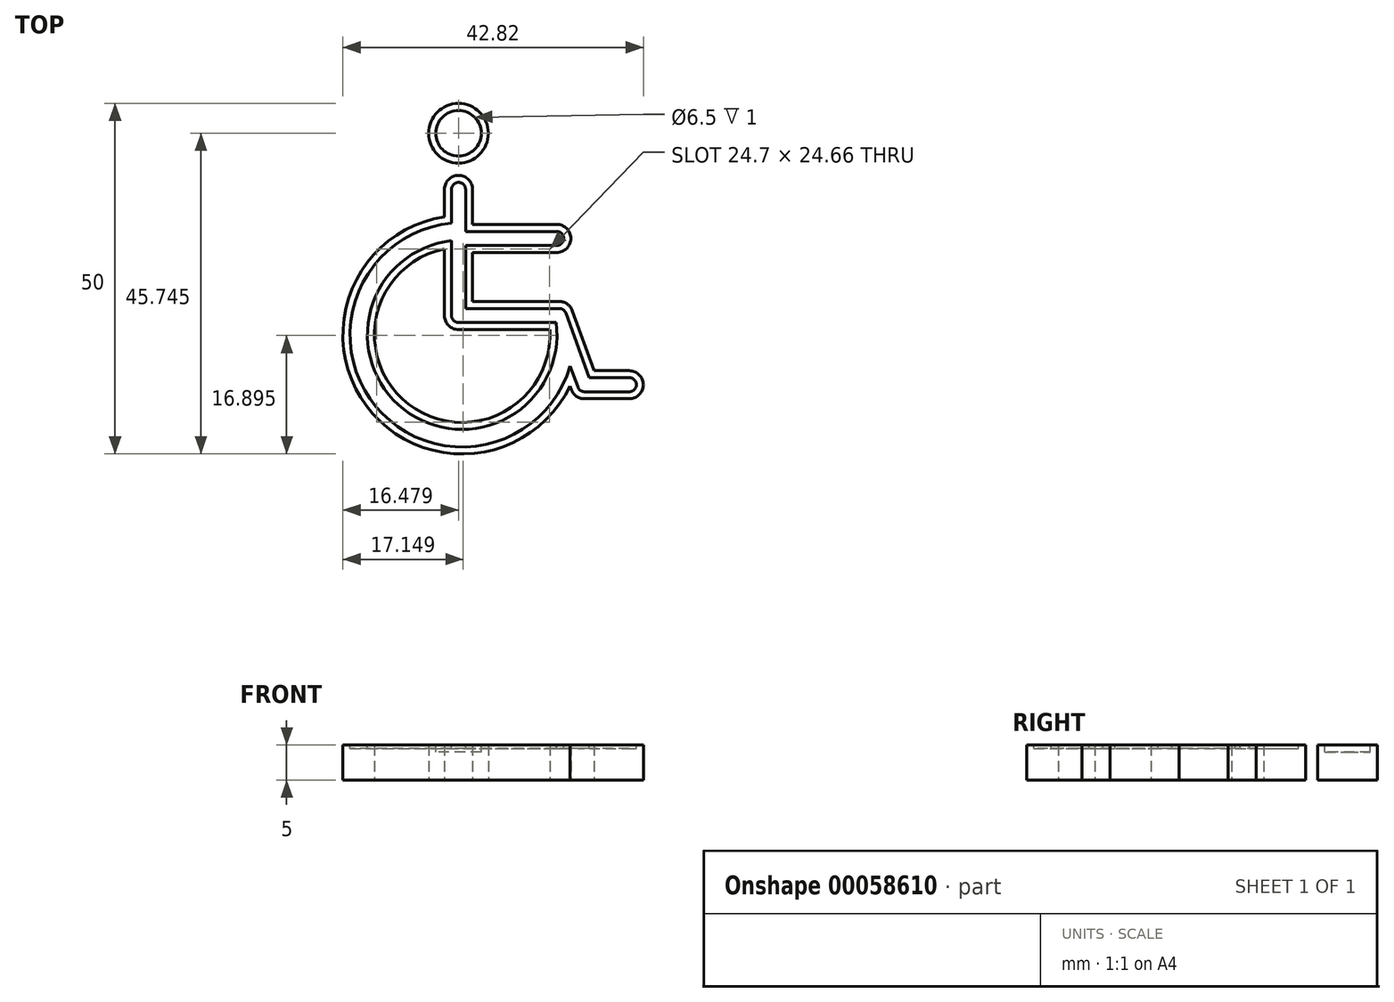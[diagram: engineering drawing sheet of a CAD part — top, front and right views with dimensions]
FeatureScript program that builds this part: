
annotation { "Feature Type Name" : "Feature", "Feature Type Description" : "" }
export const myFeature = defineFeature(function(context is Context, id is Id, definition is map)
    precondition{}
    {
        {
            var Q0;
            Q0=qCreatedBy(makeId("Top.planeOp"),FACE);
            var sketch = newSketch(context, id + "F0", { "sketchPlane" : qUnion([Q0])});
            skLineSegment(sketch, "E0", {"start": v(22.08, 21.62) * mm, "end": v(35.83, 21.62) * mm});
            skLineSegment(sketch, "E1", {"start": v(39.42, 11.75) * mm, "end": v(35.83, 21.62) * mm});
            skLineSegment(sketch, "E2", {"start": v(39.42, 11.75) * mm, "end": v(46.42, 11.75) * mm});
            skLineSegment(sketch, "E3", {"start": v(46.42, 11.75) * mm, "end": v(46.42, 7.75) * mm});
            skLineSegment(sketch, "E4", {"start": v(46.42, 7.75) * mm, "end": v(36.62, 7.75) * mm});
            skLineSegment(sketch, "E5", {"start": v(36.62, 7.75) * mm, "end": v(35.96, 9.57) * mm});
            skLineSegment(sketch, "E6", {"start": v(22.08, 21.62) * mm, "end": v(22.08, 28.62) * mm});
            skLineSegment(sketch, "E7", {"start": v(22.08, 28.62) * mm, "end": v(36.08, 28.62) * mm});
            skLineSegment(sketch, "E8", {"start": v(36.08, 28.62) * mm, "end": v(36.08, 32.62) * mm});
            skLineSegment(sketch, "E9", {"start": v(36.08, 32.62) * mm, "end": v(22.08, 32.62) * mm});
            skLineSegment(sketch, "E10", {"start": v(22.08, 32.62) * mm, "end": v(22.08, 39.62) * mm});
            skLineSegment(sketch, "E11", {"start": v(18.08, 29.12) * mm, "end": v(18.08, 17.62) * mm});
            skLineSegment(sketch, "E12", {"start": v(33.08, 17.62) * mm, "end": v(18.08, 17.62) * mm});
            skArc(sketch, "E13", {"start": v(18.08, 33.68) * mm, "mid": v(6.95, 6.75) * mm, "end": v(35.96, 9.57) * mm});
            skArc(sketch, "E14", {"start": v(18.08, 29.12) * mm, "mid": v(13, 6.95) * mm, "end": v(33.08, 17.62) * mm});
            skCircle(sketch, "E15", {"center": v(20.08, 45.62) * mm, "radius": 4.25 * mm});
            skLineSegment(sketch, "E16", {"start": v(18.08, 33.68) * mm, "end": v(18.08, 39.62) * mm});
            skLineSegment(sketch, "E17", {"start": v(22.08, 39.62) * mm, "end": v(18.08, 39.62) * mm});
            skSolve(sketch);
        }
        {
            var Q0;
            Q0=makeQuery(id+"F0.imprint","IMPRINT",FACE,{"disambiguationData":[TD([[makeQuery(id+"F0.imprint","IMPRINT",EDGE,{"derivedFrom":sQuery(id+"F0.wireOp",EDGE,"E0")}),-1.0]])]});
            var Q1;
            Q1=makeQuery(id+"F0.imprint","IMPRINT",FACE,{"disambiguationData":[TD([[makeQuery(id+"F0.imprint","IMPRINT",EDGE,{"derivedFrom":sQuery(id+"F0.wireOp",EDGE,"E15")}),1.0]])]});
            extrude(context, id + "F1", {"entities" : qUnion([Q0, Q1]), "depth" : 5 * mm});
        }
        {
            var Q0;
            Q0=makeQuery(id+"F1.opExtrude","SWEPT_EDGE",EDGE,{"disambiguationData":[OSD([sQuery(id+"F0.wireOp",EDGE,"E16"),sQuery(id+"F0.wireOp",EDGE,"E17")])]});
            var Q1;
            Q1=makeQuery(id+"F1.opExtrude","SWEPT_EDGE",EDGE,{"disambiguationData":[OSD([sQuery(id+"F0.wireOp",EDGE,"E10"),sQuery(id+"F0.wireOp",EDGE,"E17")])]});
            var Q2;
            Q2=makeQuery(id+"F1.opExtrude","SWEPT_EDGE",EDGE,{"disambiguationData":[OSD([sQuery(id+"F0.wireOp",EDGE,"E0"),sQuery(id+"F0.wireOp",EDGE,"E1")])]});
            var Q3;
            Q3=makeQuery(id+"F1.opExtrude","SWEPT_EDGE",EDGE,{"disambiguationData":[OSD([sQuery(id+"F0.wireOp",EDGE,"E7"),sQuery(id+"F0.wireOp",EDGE,"E8")])]});
            var Q4;
            Q4=makeQuery(id+"F1.opExtrude","SWEPT_EDGE",EDGE,{"disambiguationData":[OSD([sQuery(id+"F0.wireOp",EDGE,"E8"),sQuery(id+"F0.wireOp",EDGE,"E9")])]});
            var Q5;
            Q5=makeQuery(id+"F1.opExtrude","SWEPT_EDGE",EDGE,{"disambiguationData":[OSD([sQuery(id+"F0.wireOp",EDGE,"E2"),sQuery(id+"F0.wireOp",EDGE,"E3")])]});
            var Q6;
            Q6=makeQuery(id+"F1.opExtrude","SWEPT_EDGE",EDGE,{"disambiguationData":[OSD([sQuery(id+"F0.wireOp",EDGE,"E3"),sQuery(id+"F0.wireOp",EDGE,"E4")])]});
            var Q7;
            Q7=makeQuery(id+"F1.opExtrude","SWEPT_EDGE",EDGE,{"disambiguationData":[OSD([sQuery(id+"F0.wireOp",EDGE,"E11"),sQuery(id+"F0.wireOp",EDGE,"E12")])]});
            var Q8;
            Q8=makeQuery(id+"F1.opExtrude","SWEPT_EDGE",EDGE,{"disambiguationData":[OSD([sQuery(id+"F0.wireOp",EDGE,"E4"),sQuery(id+"F0.wireOp",EDGE,"E5")])]});
            fillet(context, id + "F2", {"entities" : qUnion([Q0, Q1, Q2, Q3, Q4, Q5, Q6, Q7, Q8]), "radius" : 2 * mm, "tangentPropagation" : true, "allowEdgeOverflow" : false});
        }
        {
            var Q0;
            Q0=makeQuery(id+"F1.opExtrude","CAP_FACE",FACE,{"disambiguationData":[OSD([sQuery(id+"F0.wireOp",EDGE,"E0"),sQuery(id+"F0.wireOp",EDGE,"E1"),sQuery(id+"F0.wireOp",EDGE,"E2"),sQuery(id+"F0.wireOp",EDGE,"E3"),sQuery(id+"F0.wireOp",EDGE,"E4"),sQuery(id+"F0.wireOp",EDGE,"E5"),sQuery(id+"F0.wireOp",EDGE,"E6"),sQuery(id+"F0.wireOp",EDGE,"E7"),sQuery(id+"F0.wireOp",EDGE,"E8"),sQuery(id+"F0.wireOp",EDGE,"E9"),sQuery(id+"F0.wireOp",EDGE,"E10"),sQuery(id+"F0.wireOp",EDGE,"E11"),sQuery(id+"F0.wireOp",EDGE,"E12"),sQuery(id+"F0.wireOp",EDGE,"E13"),sQuery(id+"F0.wireOp",EDGE,"E14"),sQuery(id+"F0.wireOp",EDGE,"E16"),sQuery(id+"F0.wireOp",EDGE,"E17")])],"isStart":false});
            var sketch = newSketch(context, id + "F3", { "sketchPlane" : qUnion([Q0])});
            skLineSegment(sketch, "E18.0", {"start": v(19.08, 32.8) * mm, "end": v(19.08, 37.62) * mm});
            skArc(sketch, "E18.1", {"start": v(21.08, 37.62) * mm, "mid": v(20.08, 38.62) * mm, "end": v(19.08, 37.62) * mm});
            skLineSegment(sketch, "E18.2", {"start": v(21.08, 31.62) * mm, "end": v(21.08, 37.62) * mm});
            skLineSegment(sketch, "E18.3", {"start": v(34.08, 31.62) * mm, "end": v(21.08, 31.62) * mm});
            skArc(sketch, "E18.4", {"start": v(34.08, 29.62) * mm, "mid": v(35.08, 30.62) * mm, "end": v(34.08, 31.62) * mm});
            skArc(sketch, "E18.5", {"start": v(44.42, 8.75) * mm, "mid": v(45.42, 9.75) * mm, "end": v(44.42, 10.75) * mm});
            skLineSegment(sketch, "E18.6", {"start": v(44.42, 8.75) * mm, "end": v(38.02, 8.75) * mm});
            skArc(sketch, "E18.7", {"start": v(37.08, 9.4) * mm, "mid": v(37.45, 8.93) * mm, "end": v(38.02, 8.75) * mm});
            skLineSegment(sketch, "E18.8", {"start": v(37.08, 9.4) * mm, "end": v(35.98, 12.44) * mm});
            skLineSegment(sketch, "E18.9", {"start": v(38.72, 10.75) * mm, "end": v(44.42, 10.75) * mm});
            skLineSegment(sketch, "E18.10", {"start": v(38.72, 10.75) * mm, "end": v(35.37, 19.96) * mm});
            skArc(sketch, "E18.11", {"start": v(35.37, 19.96) * mm, "mid": v(35, 20.43) * mm, "end": v(34.43, 20.62) * mm});
            skLineSegment(sketch, "E18.12", {"start": v(21.08, 20.62) * mm, "end": v(34.43, 20.62) * mm});
            skLineSegment(sketch, "E18.13", {"start": v(21.08, 20.62) * mm, "end": v(21.08, 29.62) * mm});
            skArc(sketch, "E18.14", {"start": v(19.08, 32.8) * mm, "mid": v(8.29, 6.65) * mm, "end": v(35.98, 12.44) * mm});
            skLineSegment(sketch, "E18.15", {"start": v(21.08, 29.62) * mm, "end": v(34.08, 29.62) * mm});
            skArc(sketch, "E19.0", {"start": v(19.08, 30.29) * mm, "mid": v(12.28, 6.24) * mm, "end": v(33.99, 18.62) * mm});
            skLineSegment(sketch, "E19.1", {"start": v(19.08, 30.29) * mm, "end": v(19.08, 18.62) * mm});
            skLineSegment(sketch, "E19.2", {"start": v(33.99, 18.62) * mm, "end": v(19.08, 18.62) * mm});
            skCircle(sketch, "E20.0", {"center": v(20.08, 45.62) * mm, "radius": 3.25 * mm});
            skSolve(sketch);
        }
        {
            var Q0;
            Q0=makeQuery(id+"F3.imprint","IMPRINT",FACE,{"disambiguationData":[TD([[makeQuery(id+"F3.imprint","IMPRINT",EDGE,{"derivedFrom":sQuery(id+"F3.wireOp",EDGE,"E18.0")}),-1.0]])]});
            var Q1;
            Q1=makeQuery(id+"F3.imprint","IMPRINT",FACE,{"disambiguationData":[TD([[makeQuery(id+"F3.imprint","IMPRINT",EDGE,{"derivedFrom":sQuery(id+"F3.wireOp",EDGE,"E20.0")}),1.0]])]});
            extrude(context, id + "F4", {"entities" : qUnion([Q0, Q1]), "operationType" : NewBodyOperationType.REMOVE, "oppositeDirection" : true, "depth" : 0.5 * mm});
        }
        {
            var Q0;
            Q0=makeQuery(id+"F4.boolean.opBoolean","COPY",EDGE,{"derivedFrom":makeQuery(id+"F4.opExtrude","SWEPT_EDGE",EDGE,{"disambiguationData":[OSD([sQuery(id+"F3.wireOp",EDGE,"E19.1"),sQuery(id+"F3.wireOp",EDGE,"E19.2")])]})});
            fillet(context, id + "F5", {"entities" : qUnion([Q0]), "radius" : 1 * mm, "tangentPropagation" : true, "allowEdgeOverflow" : false});
        }
        {
            var Q0;
            Q0=makeQuery(id+"F1.opExtrude","CAP_FACE",FACE,{"disambiguationData":[OSD([sQuery(id+"F0.wireOp",EDGE,"E15")])],"isStart":false});
            var sketch = newSketch(context, id + "F6", { "sketchPlane" : qUnion([Q0])});
            skCircle(sketch, "E21.0", {"center": v(20.08, 45.62) * mm, "radius": 3.25 * mm});
            skSolve(sketch);
        }
        {
            var Q0;
            Q0=makeQuery(id+"F6.imprint","IMPRINT",FACE,{"disambiguationData":[TD([[makeQuery(id+"F6.imprint","IMPRINT",EDGE,{"derivedFrom":sQuery(id+"F6.wireOp",EDGE,"E21.0")}),1.0]])]});
            extrude(context, id + "F7", {"entities" : qUnion([Q0]), "operationType" : NewBodyOperationType.REMOVE, "oppositeDirection" : true, "depth" : 1 * mm});
        }
    });
